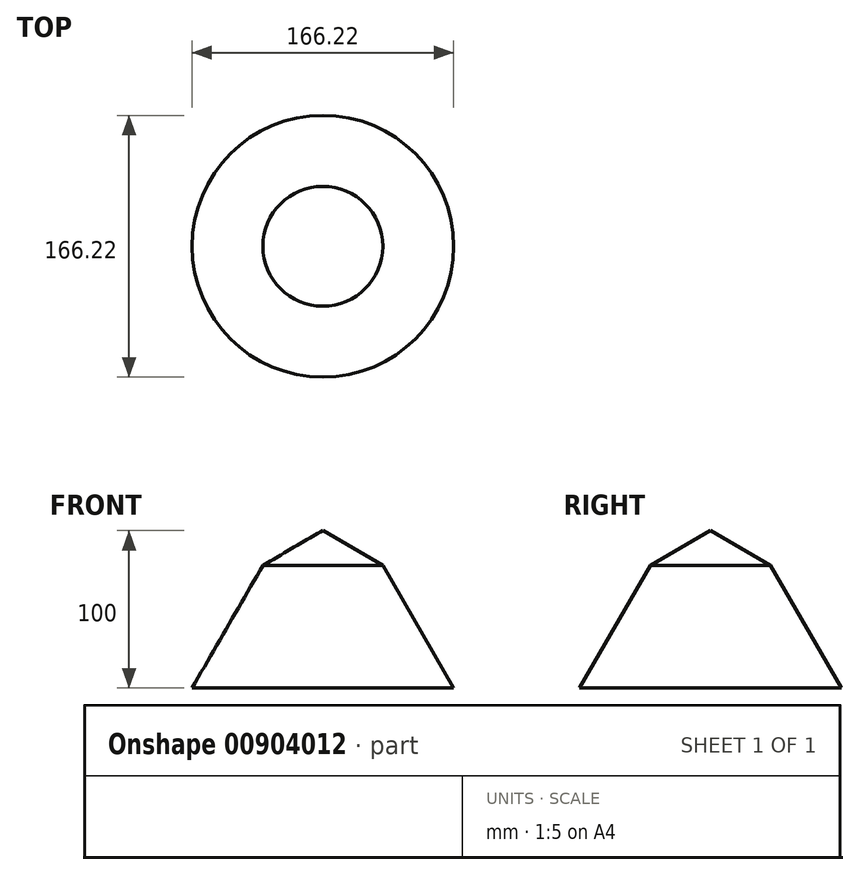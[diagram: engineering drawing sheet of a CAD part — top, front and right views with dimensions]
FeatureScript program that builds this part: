
annotation { "Feature Type Name" : "Feature", "Feature Type Description" : "" }
export const myFeature = defineFeature(function(context is Context, id is Id, definition is map)
    precondition{}
    {
        {
            var Q0;
            Q0=qCreatedBy(makeId("Front.planeOp"),FACE);
            var sketch = newSketch(context, id + "F0", { "sketchPlane" : qUnion([Q0])});
            skLineSegment(sketch, "E0", {"start": v(0, 0) * mm, "end": v(0, 100) * mm});
            skLineSegment(sketch, "E1", {"start": v(0, 100) * mm, "end": v(38.06, 78.03) * mm});
            skLineSegment(sketch, "E2", {"start": v(38.06, 78.03) * mm, "end": v(83.1, 0) * mm});
            skLineSegment(sketch, "E3", {"start": v(83.1, 0) * mm, "end": v(0, 0) * mm});
            skSolve(sketch);
        }
        {
            var Q0;
            Q0=makeQuery(id+"F0.imprint","IMPRINT",FACE,{"disambiguationData":[TD([[makeQuery(id+"F0.imprint","IMPRINT",EDGE,{"derivedFrom":sQuery(id+"F0.wireOp",EDGE,"E0")}),-1.0]])]});
            var Q1;
            Q1=sQuery(id+"F0.wireOp",EDGE,"E0");
            revolve(context, id + "F1", {"surfaceOperationType" : NewSurfaceOperationType.NEW, "entities" : qUnion([Q0]), "axis" : qUnion([Q1]), "revolveType" : RevolveType.FULL});
        }
        {
            var Q0;
            Q0=qCreatedBy(makeId("Right.planeOp"),FACE);
            cPlane(context, id + "F2", {"entities" : qUnion([Q0]), "cplaneType" : CPlaneType.OFFSET, "offset" : 10 * mm, "width" : 152.4 * mm, "height" : 152.4 * mm});
        }
    });
